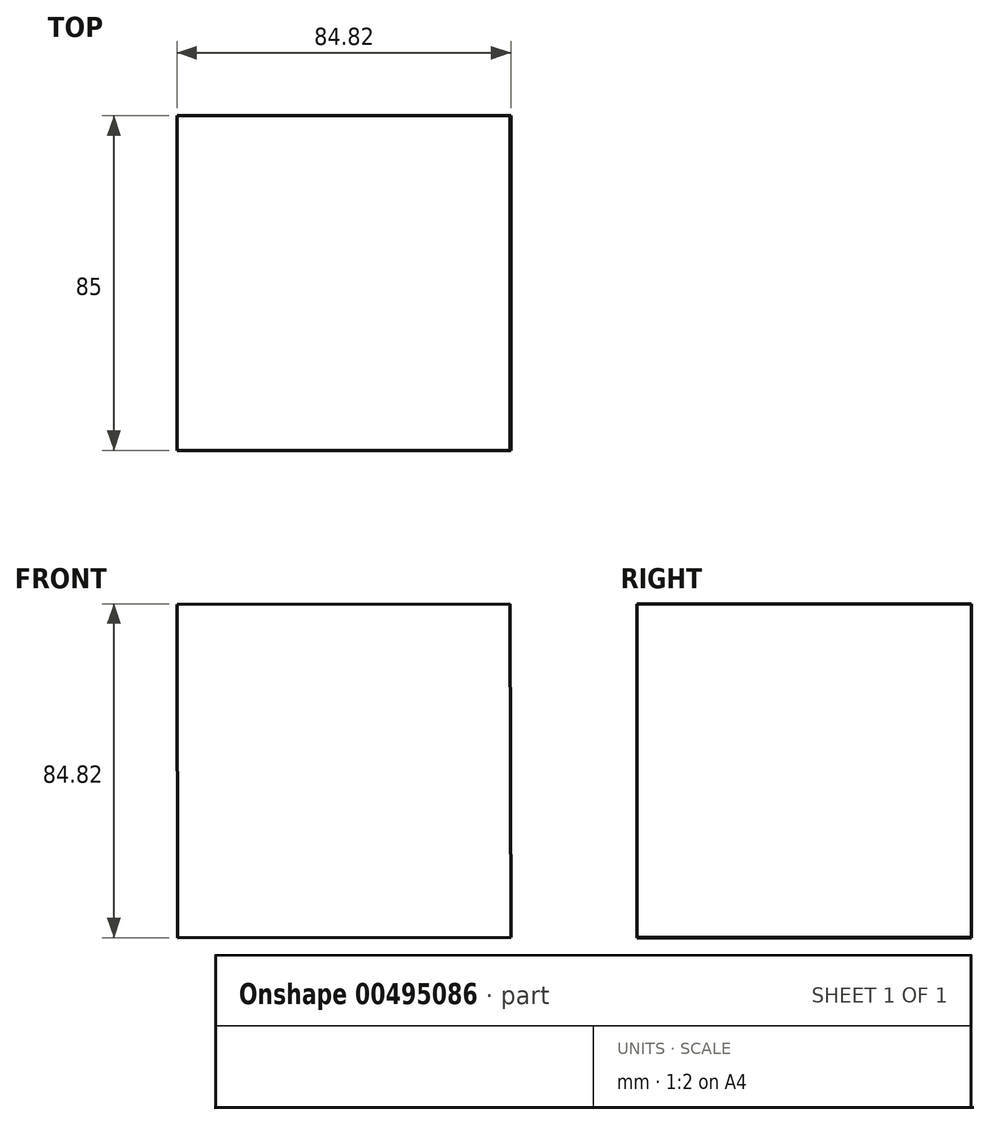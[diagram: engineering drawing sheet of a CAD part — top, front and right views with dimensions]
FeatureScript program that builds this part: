
annotation { "Feature Type Name" : "Feature", "Feature Type Description" : "" }
export const myFeature = defineFeature(function(context is Context, id is Id, definition is map)
    precondition{}
    {
        {
            var Q0;
            Q0=qCreatedBy(makeId("Front.planeOp"),FACE);
            var sketch = newSketch(context, id + "F0", { "sketchPlane" : qUnion([Q0])});
            skCircle(sketch, "E0.cCircle", {"center": v(0, 0) * mm, "radius": 59.87 * mm, "construction": true});
            skLineSegment(sketch, "E0.0", {"start": v(42.26, 42.4) * mm, "end": v(-42.4, 42.26) * mm});
            skLineSegment(sketch, "E0.1", {"start": v(42.4, -42.26) * mm, "end": v(42.26, 42.4) * mm});
            skLineSegment(sketch, "E0.2", {"start": v(-42.26, -42.4) * mm, "end": v(42.4, -42.26) * mm});
            skLineSegment(sketch, "E0.3", {"start": v(-42.4, 42.26) * mm, "end": v(-42.26, -42.4) * mm});
            skSolve(sketch);
        }
        {
            var Q0;
            Q0=makeQuery(id+"F0.imprint","IMPRINT",FACE,{"disambiguationData":[TD([[makeQuery(id+"F0.imprint","IMPRINT",EDGE,{"derivedFrom":sQuery(id+"F0.wireOp",EDGE,"E0.0")}),1.0]])]});
            extrude(context, id + "F1", {"entities" : qUnion([Q0]), "depth" : 85 * mm});
        }
    });
